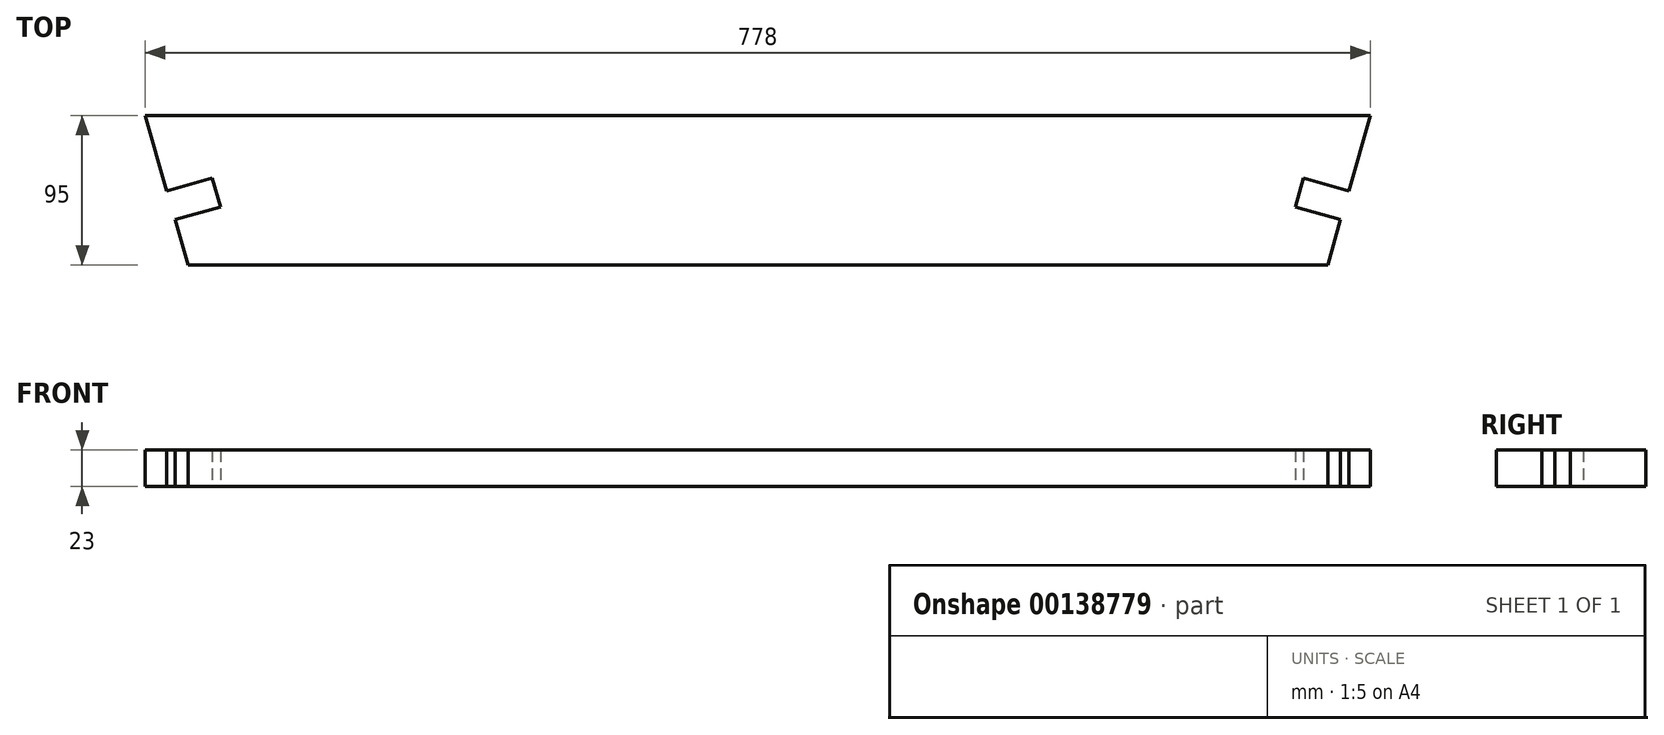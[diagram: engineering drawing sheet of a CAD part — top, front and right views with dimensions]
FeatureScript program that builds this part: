
annotation { "Feature Type Name" : "Feature", "Feature Type Description" : "" }
export const myFeature = defineFeature(function(context is Context, id is Id, definition is map)
    precondition{}
    {
        {
            var Q0;
            Q0=qCreatedBy(makeId("Top.planeOp"),FACE);
            var sketch = newSketch(context, id + "F0", { "sketchPlane" : qUnion([Q0])});
            skLineSegment(sketch, "E0", {"start": v(-361.94, 0) * mm, "end": v(-370.16, 28.85) * mm});
            skLineSegment(sketch, "E1", {"start": v(-370.16, 28.85) * mm, "end": v(-341.3, 37.07) * mm});
            skLineSegment(sketch, "E2", {"start": v(-341.3, 37.07) * mm, "end": v(-346.51, 55.34) * mm});
            skLineSegment(sketch, "E3", {"start": v(-346.51, 55.34) * mm, "end": v(-375.36, 47.13) * mm});
            skLineSegment(sketch, "E4.trimOffspring", {"start": v(-375.36, 47.13) * mm, "end": v(-389, 95) * mm});
            skLineSegment(sketch, "E5.MirrorCS", {"start": v(361.94, 0) * mm, "end": v(370.16, 28.85) * mm});
            skLineSegment(sketch, "E6.MirrorCS", {"start": v(370.16, 28.85) * mm, "end": v(341.3, 37.07) * mm});
            skLineSegment(sketch, "E7.MirrorCS", {"start": v(341.3, 37.07) * mm, "end": v(346.51, 55.34) * mm});
            skLineSegment(sketch, "E8.MirrorCS", {"start": v(346.51, 55.34) * mm, "end": v(375.36, 47.13) * mm});
            skLineSegment(sketch, "E9.MirrorCS", {"start": v(375.36, 47.13) * mm, "end": v(389, 95) * mm});
            skLineSegment(sketch, "E10", {"start": v(-389, 95) * mm, "end": v(389, 95) * mm});
            skLineSegment(sketch, "E11", {"start": v(-361.94, 0) * mm, "end": v(361.94, 0) * mm});
            skSolve(sketch);
        }
        {
            var Q0;
            Q0 = qSketchRegion(id + "F0", true);
            extrude(context, id + "F1", {"entities" : qUnion([Q0]), "endBound" : BoundingType.SYMMETRIC, "depth" : 23 * mm});
        }
    });
